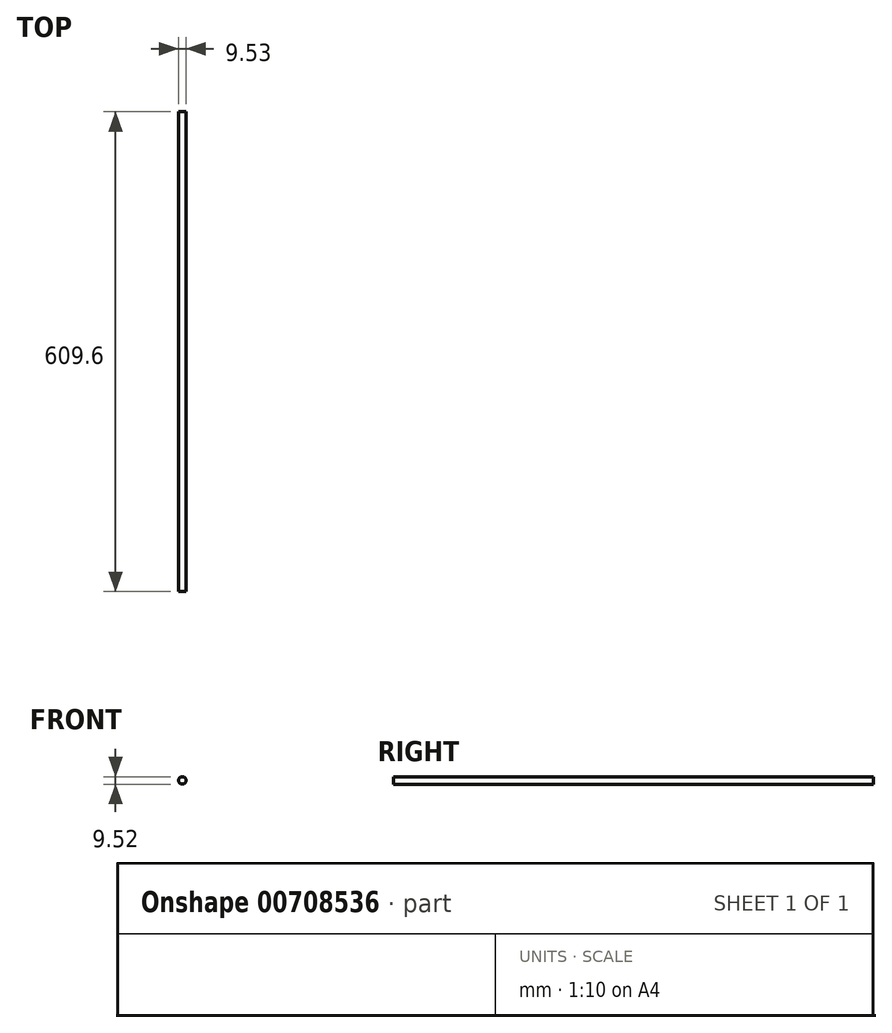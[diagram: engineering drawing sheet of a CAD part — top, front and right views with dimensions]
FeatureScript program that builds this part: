
annotation { "Feature Type Name" : "Feature", "Feature Type Description" : "" }
export const myFeature = defineFeature(function(context is Context, id is Id, definition is map)
    precondition{}
    {
        {
            var Q0;
            Q0=qCreatedBy(makeId("Front.planeOp"),FACE);
            var sketch = newSketch(context, id + "F0", { "sketchPlane" : qUnion([Q0])});
            skCircle(sketch, "E0", {"center": v(25.89, 45.23) * mm, "radius": 4.76 * mm});
            skSolve(sketch);
        }
        {
            var Q0;
            Q0=makeQuery(id+"F0.imprint","IMPRINT",FACE,{"disambiguationData":[TD([[makeQuery(id+"F0.imprint","IMPRINT",EDGE,{"derivedFrom":sQuery(id+"F0.wireOp",EDGE,"E0")}),1.0]])]});
            extrude(context, id + "F1", {"entities" : qUnion([Q0]), "depth" : 609.6 * mm, "offsetDistance" : 25.4 * mm});
        }
    });
